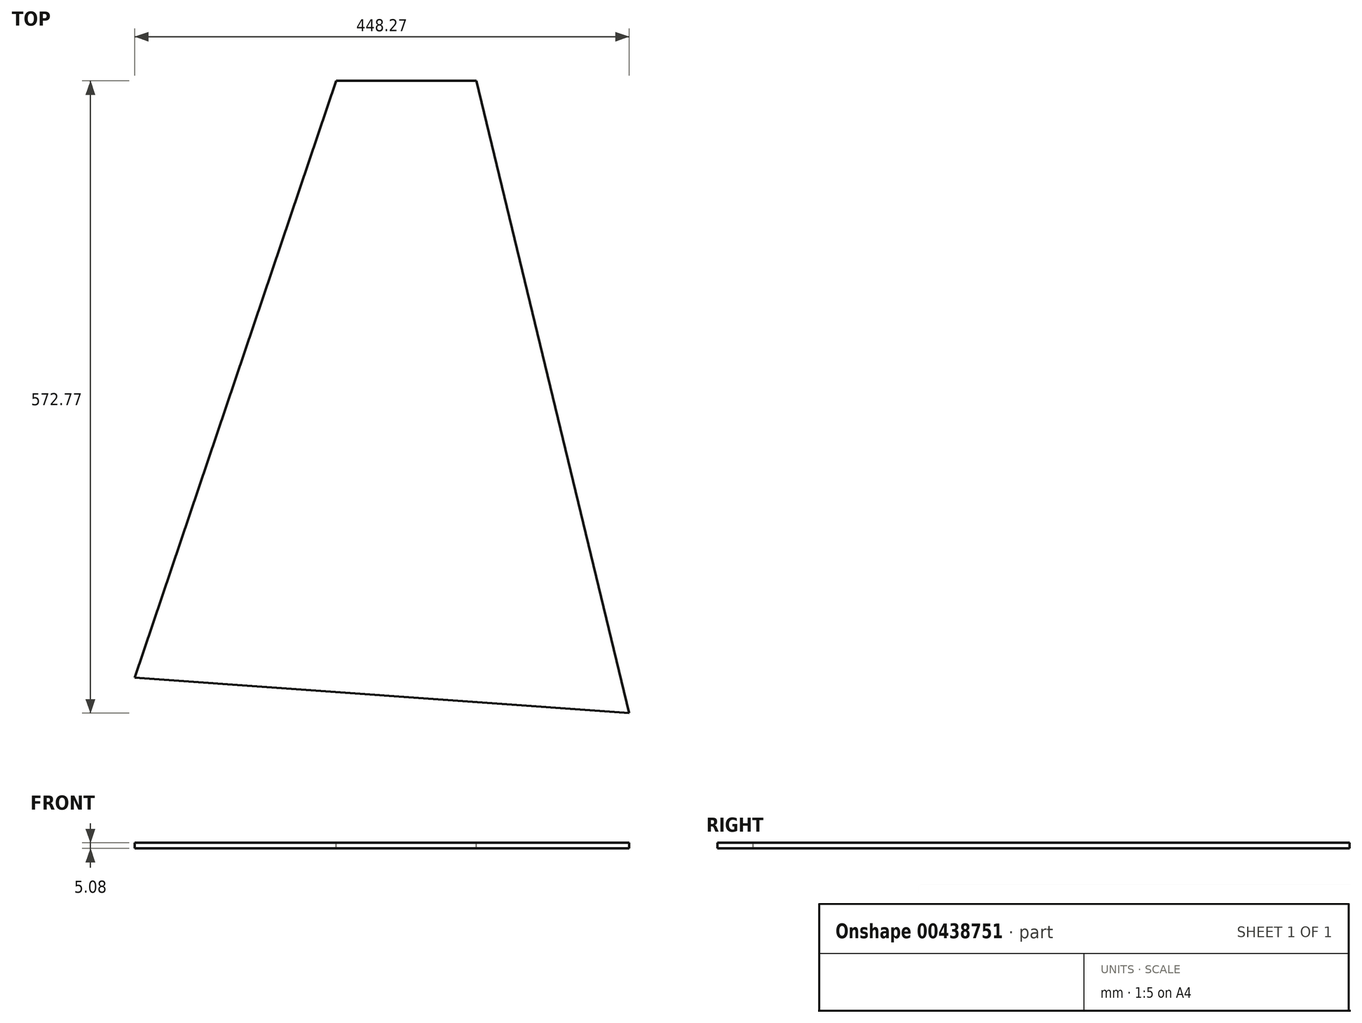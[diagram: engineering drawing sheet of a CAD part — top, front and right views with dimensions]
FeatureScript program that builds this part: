
annotation { "Feature Type Name" : "Feature", "Feature Type Description" : "" }
export const myFeature = defineFeature(function(context is Context, id is Id, definition is map)
    precondition{}
    {
        {
            var Q0;
            Q0=qCreatedBy(makeId("Top.planeOp"),FACE);
            var sketch = newSketch(context, id + "F0", { "sketchPlane" : qUnion([Q0])});
            skLineSegment(sketch, "E0", {"start": v(69.72, 275.85) * mm, "end": v(208.25, -296.92) * mm});
            skLineSegment(sketch, "E1", {"start": v(208.25, -296.92) * mm, "end": v(-240.02, -264.71) * mm});
            skLineSegment(sketch, "E2", {"start": v(-240.02, -264.71) * mm, "end": v(-57.28, 275.85) * mm});
            skLineSegment(sketch, "E3", {"start": v(-57.28, 275.85) * mm, "end": v(69.72, 275.85) * mm});
            skSolve(sketch);
        }
        {
            var Q0;
            Q0 = qSketchRegion(id + "F0", true);
            extrude(context, id + "F1", {"entities" : qUnion([Q0]), "oppositeDirection" : true, "depth" : 5.08 * mm});
        }
    });
